# Revit family: Echo Eliminator - Ceiling and Wall Panels
name_source: partatom
category: Specialty Equipment
units: mm (PartAtom-declared; Revit-internal decimal feet)

## family parameters
Always vertical = No
Cut with Voids When Loaded = No
Enable Cutting in Views = Yes
Maintain Annotation Orientation = No
OmniClass Number = 23.35.00.00
OmniClass Title = Covering, Cladding, and Finishes
Part Type = Normal
Room Calculation Point = No
Round Connector Dimension = Use Diameter
Shared = No
Work Plane-Based = Yes

## types (46) — shared parameters
A = 0' - 0"
Acoustics - NRC = Sound absorption varies from NRC 0.45 to 0.95 based on installation method used when tested per ASTM C423.
Assembly Code = C30
Default Elevation = 4' - 0"
Description = Acoustic Panels
Fire Rating = ASTM E84 - Class A
Manufacturer = Acoustical Surfaces, Inc.
Material = Echo Eliminator
Model = Echo Eliminator - Ceiling and Wall Acoustical Panels
Recycled Content Percentage = 0%
Type Comments = Acoustic panels for vertical and horizontal surfaces
URL = https://www.acousticalsurfaces.com

## per-type parameters (varying)
| type | Finish | Length | T | Thickness Options | Width | ‍      1. Thickness 1" | ‍      2. Thickness 2" |
| 1 INCH THICK - 24x48 - Grey | <By Category> | 4' - 0" | 0' - 1" | 1 | 2' - 0" | Yes | No |
| 1 INCH THICK - 48X96 - Black | Paint - Acoustical-Surfaces - Echo Eliminator - Black | 8' - 0" | 0' - 1" | 1 | 4' - 0" | Yes | No |
| 1 INCH THICK - 48X96 - White | Paint - Acoustical-Surfaces - Echo Eliminator - White | 8' - 0" | 0' - 1" | 1 | 4' - 0" | Yes | No |
| 2 INCH THICK - 48X96 - Black | Paint - Acoustical-Surfaces - Echo Eliminator - Black | 8' - 0" | 0' - 2" | 2 | 4' - 0" | No | Yes |
| 2 INCH THICK - 48X96 - Beige | Paint - Acoustical-Surfaces - Echo Eliminator - Beige | 8' - 0" | 0' - 2" | 2 | 4' - 0" | No | Yes |
| 2 INCH THICK - 48X96 - White | Paint - Acoustical-Surfaces - Echo Eliminator - White | 8' - 0" | 0' - 2" | 2 | 4' - 0" | No | Yes |
| 2 INCH THICK - 24x48 - Charcoal | Paint - Acoustical-Surfaces - Echo Eliminator - Charcoal | 4' - 0" | 0' - 2" | 2 | 2' - 0" | No | Yes |
| 2 INCH THICK - 24x48 - Black | Paint - Acoustical-Surfaces - Echo Eliminator - Black | 4' - 0" | 0' - 2" | 2 | 2' - 0" | No | Yes |
| 2 INCH THICK - 24x48 - White | Paint - Acoustical-Surfaces - Echo Eliminator - White | 4' - 0" | 0' - 2" | 2 | 2' - 0" | No | Yes |
| 1 INCH THICK - 24x48 - Charcoal | Paint - Acoustical-Surfaces - Echo Eliminator - Charcoal | 4' - 0" | 0' - 1" | 1 | 2' - 0" | Yes | No |
| 1 INCH THICK - 24x48 - Black | Paint - Acoustical-Surfaces - Echo Eliminator - Black | 4' - 0" | 0' - 1" | 1 | 2' - 0" | Yes | No |
| 1 INCH THICK - 24x48 - Beige | Paint - Acoustical-Surfaces - Echo Eliminator - Beige | 4' - 0" | 0' - 1" | 1 | 2' - 0" | Yes | No |
| 1 INCH THICK - 24x48 - White | Paint - Acoustical-Surfaces - Echo Eliminator - White | 4' - 0" | 0' - 1" | 1 | 2' - 0" | Yes | No |
| 2 INCH THICK - 24x48 - Beige | Paint - Acoustical-Surfaces - Echo Eliminator - Beige | 4' - 0" | 0' - 2" | 2 | 2' - 0" | No | Yes |
| 1 INCH THICK - 24x48 - Marble Blue | Paint - Acoustical-Surfaces - Echo Eliminator - Marble Blue | 4' - 0" | 0' - 1" | 1 | 2' - 0" | Yes | No |
| 2 INCH THICK - 48x48 - Black | Paint - Acoustical-Surfaces - Echo Eliminator - Black | 4' - 0" | 0' - 2" | 2 | 4' - 0" | No | Yes |
| 2 INCH THICK - 48x48 - Charcoal | Paint - Acoustical-Surfaces - Echo Eliminator - Charcoal | 4' - 0" | 0' - 2" | 2 | 4' - 0" | No | Yes |
| 2 INCH THICK - 48x48 - Gray | <By Category> | 4' - 0" | 0' - 2" | 2 | 4' - 0" | No | Yes |
| 2 INCH THICK - 48x48 - Marble Blue | Paint - Acoustical-Surfaces - Echo Eliminator - Marble Blue | 4' - 0" | 0' - 2" | 2 | 4' - 0" | No | Yes |
| 2 INCH THICK - 48x48 - Beige | Paint - Acoustical-Surfaces - Echo Eliminator - Beige | 4' - 0" | 0' - 2" | 2 | 4' - 0" | No | Yes |
| 2 INCH THICK - 48x48 - White | Paint - Acoustical-Surfaces - Echo Eliminator - White | 4' - 0" | 0' - 2" | 2 | 4' - 0" | No | Yes |
| 1 INCH THICK - 48x48 - Black | Paint - Acoustical-Surfaces - Echo Eliminator - Black | 4' - 0" | 0' - 1" | 1 | 4' - 0" | Yes | No |
| 1 INCH THICK - 48x48 - Charcoal | Paint - Acoustical-Surfaces - Echo Eliminator - Charcoal | 4' - 0" | 0' - 1" | 1 | 4' - 0" | Yes | No |
| 1 INCH THICK - 48x48 - Grey | <By Category> | 4' - 0" | 0' - 1" | 1 | 4' - 0" | Yes | No |
| 1 INCH THICK - 48x48 - Marble Blue | Paint - Acoustical-Surfaces - Echo Eliminator - Marble Blue | 4' - 0" | 0' - 1" | 1 | 4' - 0" | Yes | No |
| 1 INCH THICK - 48x48 - Beige | Paint - Acoustical-Surfaces - Echo Eliminator - Beige | 4' - 0" | 0' - 1" | 1 | 4' - 0" | Yes | No |
| 1 INCH THICK - 48x48 - White | Paint - Acoustical-Surfaces - Echo Eliminator - White | 4' - 0" | 0' - 1" | 1 | 4' - 0" | Yes | No |
| 2 INCH THICK - 24x24 - Black | Paint - Acoustical-Surfaces - Echo Eliminator - Black | 2' - 0" | 0' - 2" | 2 | 2' - 0" | No | Yes |
| 1 INCH THICK - 24x24 - Black | Paint - Acoustical-Surfaces - Echo Eliminator - Black | 2' - 0" | 0' - 1" | 1 | 2' - 0" | Yes | No |
| 2 INCH THICK - 24x24 - Charcoal | Paint - Acoustical-Surfaces - Echo Eliminator - Charcoal | 2' - 0" | 0' - 2" | 2 | 2' - 0" | No | Yes |
| 1 INCH THICK - 24x24 - Charcoal | Paint - Acoustical-Surfaces - Echo Eliminator - Charcoal | 2' - 0" | 0' - 1" | 1 | 2' - 0" | Yes | No |
| 2 INCH THICK - 24x24 - Gray | <By Category> | 2' - 0" | 0' - 2" | 2 | 2' - 0" | No | Yes |
| 1 INCH THICK - 24x24 - Grey | <By Category> | 2' - 0" | 0' - 1" | 1 | 2' - 0" | Yes | No |
| 2 INCH THICK - 24x24 - Marble Blue | Paint - Acoustical-Surfaces - Echo Eliminator - Marble Blue | 2' - 0" | 0' - 2" | 2 | 2' - 0" | No | Yes |
| 1 INCH THICK - 24x24 - Marble Blue | Paint - Acoustical-Surfaces - Echo Eliminator - Marble Blue | 2' - 0" | 0' - 1" | 1 | 2' - 0" | Yes | No |
| 2 INCH THICK - 24x24 - Beige | Paint - Acoustical-Surfaces - Echo Eliminator - Beige | 2' - 0" | 0' - 2" | 2 | 2' - 0" | No | Yes |
| 1 INCH THICK - 24x24 - Beige | Paint - Acoustical-Surfaces - Echo Eliminator - Beige | 2' - 0" | 0' - 1" | 1 | 2' - 0" | Yes | No |
| 2 INCH THICK - 24x24 - White | Paint - Acoustical-Surfaces - Echo Eliminator - White | 2' - 0" | 0' - 2" | 2 | 2' - 0" | No | Yes |
| 1 INCH THICK - 24x24 - White | Paint - Acoustical-Surfaces - Echo Eliminator - White | 2' - 0" | 0' - 1" | 1 | 2' - 0" | Yes | No |
| 2 INCH THICK - 24x48 - Gray | <By Category> | 4' - 0" | 0' - 2" | 2 | 2' - 0" | No | Yes |
| 1 INCH THICK - 48X96 - Marble Blue | Paint - Acoustical-Surfaces - Echo Eliminator - Marble Blue | 8' - 0" | 0' - 1" | 1 | 4' - 0" | Yes | No |
| 1 INCH THICK - 48X96 - Charcoal | Paint - Acoustical-Surfaces - Echo Eliminator - Charcoal | 8' - 0" | 0' - 1" | 1 | 4' - 0" | Yes | No |
| 1 INCH THICK - 48X96 - Beige | Paint - Acoustical-Surfaces - Echo Eliminator - Beige | 8' - 0" | 0' - 1" | 1 | 4' - 0" | Yes | No |
| 2 INCH THICK - 48X96 - Marble Blue | Paint - Acoustical-Surfaces - Echo Eliminator - Marble Blue | 8' - 0" | 0' - 2" | 2 | 4' - 0" | No | Yes |
| 2 INCH THICK - 48X96 - Charcoal | Paint - Acoustical-Surfaces - Echo Eliminator - Charcoal | 8' - 0" | 0' - 2" | 2 | 4' - 0" | No | Yes |
| 2 INCH THICK - 24x48 - Marble Blue | Paint - Acoustical-Surfaces - Echo Eliminator - Marble Blue | 4' - 0" | 0' - 2" | 2 | 2' - 0" | No | Yes |

## geometry (parser evidence)
native form markers: Sweep x11
no freeform markers — native parametric forms only
